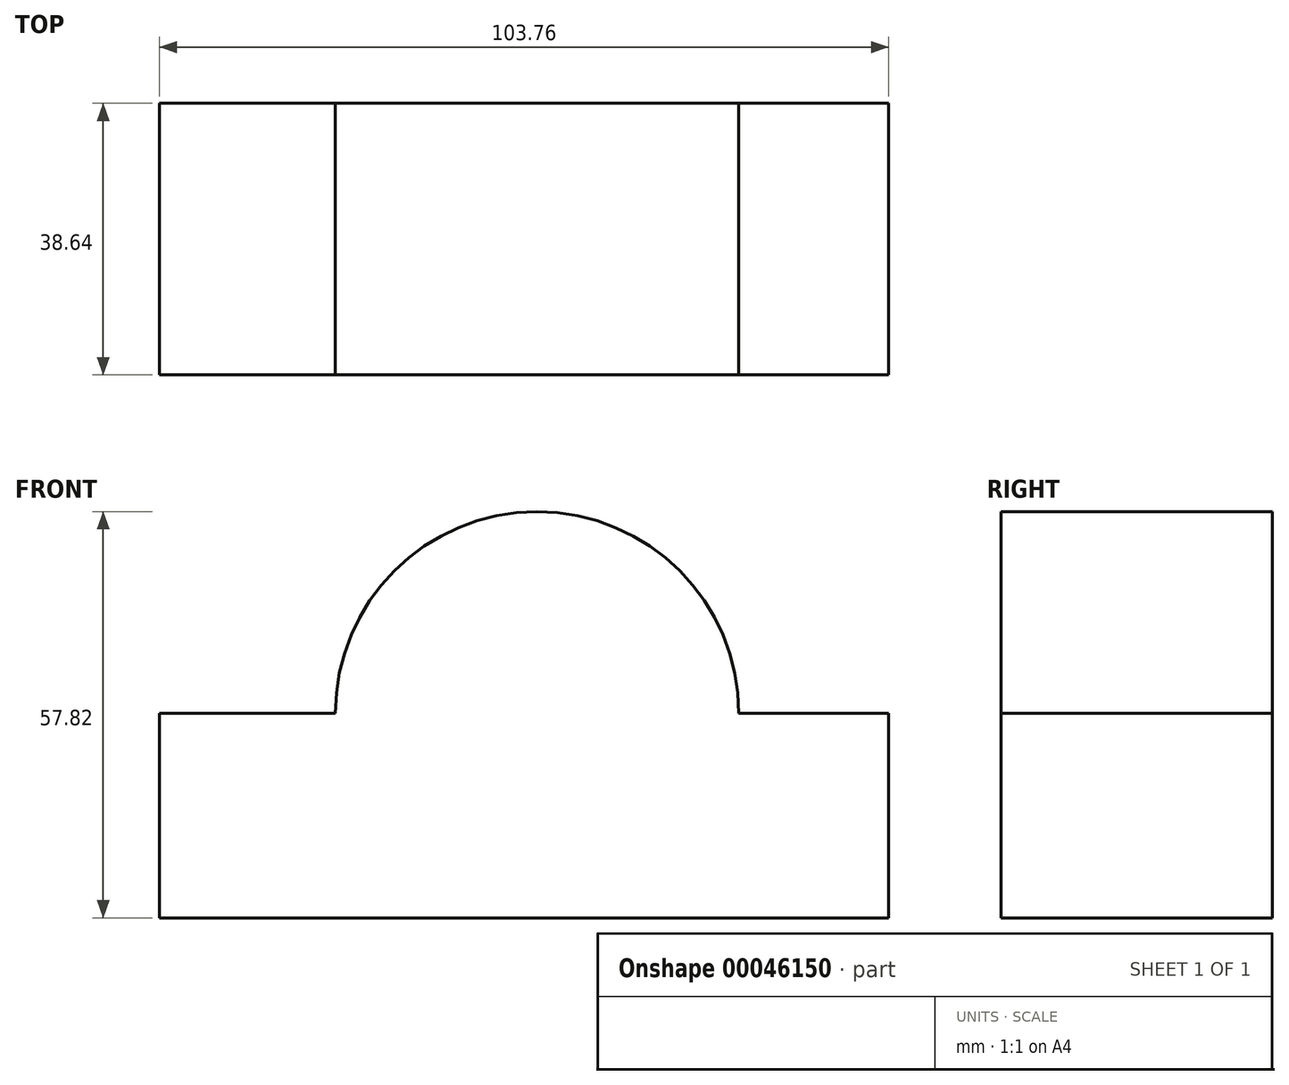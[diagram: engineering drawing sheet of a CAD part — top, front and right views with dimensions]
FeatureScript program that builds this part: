
annotation { "Feature Type Name" : "Feature", "Feature Type Description" : "" }
export const myFeature = defineFeature(function(context is Context, id is Id, definition is map)
    precondition{}
    {
        {
            var Q0;
            Q0=qCreatedBy(makeId("Front.planeOp"),FACE);
            var sketch = newSketch(context, id + "F0", { "sketchPlane" : qUnion([Q0])});
            skArc(sketch, "E0", {"start": v(28.7, 0) * mm, "mid": v(0, 28.7) * mm, "end": v(-28.7, 0) * mm});
            skLineSegment(sketch, "E1.bottom", {"start": v(-28.7, 0) * mm, "end": v(-53.73, 0) * mm});
            skLineSegment(sketch, "E1.top", {"start": v(0, -29.12) * mm, "end": v(-53.73, -29.12) * mm});
            skLineSegment(sketch, "E1.right", {"start": v(-53.73, 0) * mm, "end": v(-53.73, -29.12) * mm});
            skLineSegment(sketch, "E2.bottom", {"start": v(28.7, 0) * mm, "end": v(50.03, 0) * mm});
            skLineSegment(sketch, "E2.top", {"start": v(0, -29.12) * mm, "end": v(50.03, -29.12) * mm});
            skLineSegment(sketch, "E2.right", {"start": v(50.03, 0) * mm, "end": v(50.03, -29.12) * mm});
            skSolve(sketch);
        }
        {
            var Q0;
            Q0=makeQuery(id+"F0.imprint","IMPRINT",FACE,{"disambiguationData":[TD([[makeQuery(id+"F0.imprint","IMPRINT",EDGE,{"derivedFrom":sQuery(id+"F0.wireOp",EDGE,"E0")}),1.0]])]});
            extrude(context, id + "F1", {"entities" : qUnion([Q0]), "depth" : 38.64 * mm});
        }
    });
